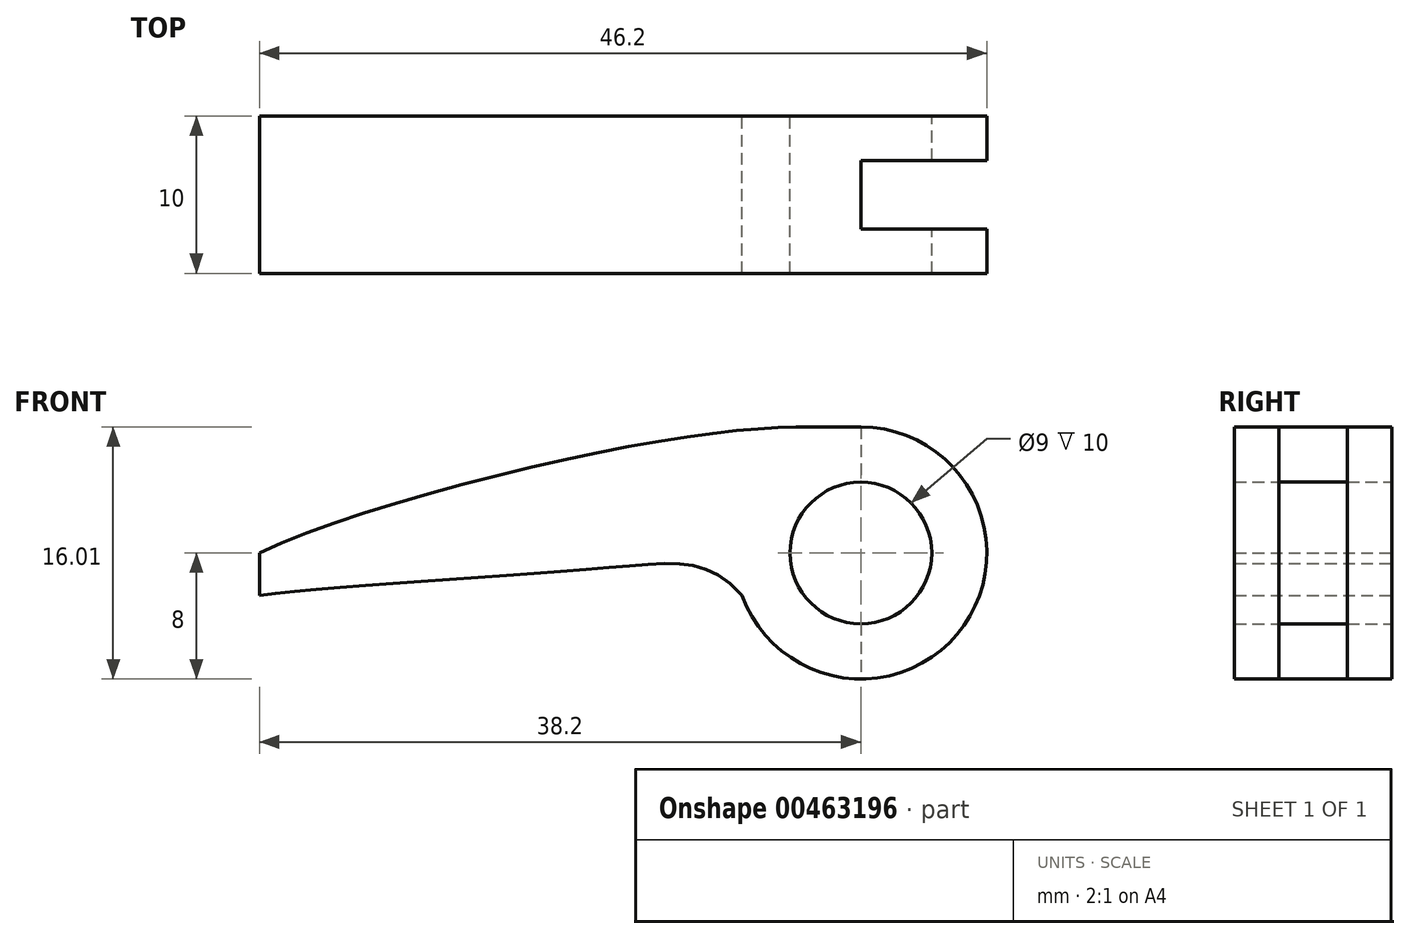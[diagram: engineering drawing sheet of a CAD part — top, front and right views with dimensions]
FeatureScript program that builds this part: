
annotation { "Feature Type Name" : "Feature", "Feature Type Description" : "" }
export const myFeature = defineFeature(function(context is Context, id is Id, definition is map)
    precondition{}
    {
        {
            var Q0;
            Q0=qCreatedBy(makeId("Front.planeOp"),FACE);
            var sketch = newSketch(context, id + "F0", { "sketchPlane" : qUnion([Q0])});
            skCircle(sketch, "E0", {"center": v(0, 0) * mm, "radius": 4.5 * mm});
            skArc(sketch, "E1", {"start": v(-7.54, -2.68) * mm, "mid": v(6.54, -4.61) * mm, "end": v(0, 8) * mm});
            skFitSpline(sketch, "E2", {"points": [v(0, 8) * mm, v(-10.47, 7.47) * mm, v(-38.2, 0) * mm], "startDerivative": vector(-22.5, 0) * mm, "endDerivative": vector(-30.17, -14.46) * mm});
            skLineSegment(sketch, "E3", {"start": v(-38.2, 0) * mm, "end": v(-38.2, -2.68) * mm});
            skFitSpline(sketch, "E4", {"points": [v(-38.2, -2.68) * mm, v(-15.43, -0.88) * mm, v(-7.54, -2.68) * mm], "startDerivative": vector(21.05, 2.65) * mm, "endDerivative": vector(18.04, -19.31) * mm});
            skSolve(sketch);
        }
        {
            var Q0;
            Q0=makeQuery(id+"F0.imprint","IMPRINT",FACE,{"disambiguationData":[TD([[makeQuery(id+"F0.imprint","IMPRINT",EDGE,{"derivedFrom":sQuery(id+"F0.wireOp",EDGE,"E0")}),-1.0]])]});
            extrude(context, id + "F1", {"entities" : qUnion([Q0]), "endBound" : BoundingType.SYMMETRIC, "depth" : 10 * mm});
        }
        {
            var Q0;
            Q0=qCreatedBy(makeId("Top.planeOp"),FACE);
            var sketch = newSketch(context, id + "F2", { "sketchPlane" : qUnion([Q0])});
            skLineSegment(sketch, "E5.bottom", {"start": v(0, 2.17) * mm, "end": v(8.89, 2.17) * mm});
            skLineSegment(sketch, "E5.top", {"start": v(0, -2.17) * mm, "end": v(8.89, -2.17) * mm});
            skLineSegment(sketch, "E5.left", {"start": v(0, 2.17) * mm, "end": v(0, -2.17) * mm});
            skLineSegment(sketch, "E5.right", {"start": v(8.89, 2.17) * mm, "end": v(8.89, -2.17) * mm});
            skPoint(sketch, "E5.middle", {"position": v(4.44, 0) * mm});
            skSolve(sketch);
        }
        {
            var Q0;
            Q0 = qSketchRegion(id + "F2", true);
            extrude(context, id + "F3", {"entities" : qUnion([Q0]), "operationType" : NewBodyOperationType.REMOVE, "endBound" : BoundingType.SYMMETRIC, "depth" : 25.4 * mm});
        }
    });
